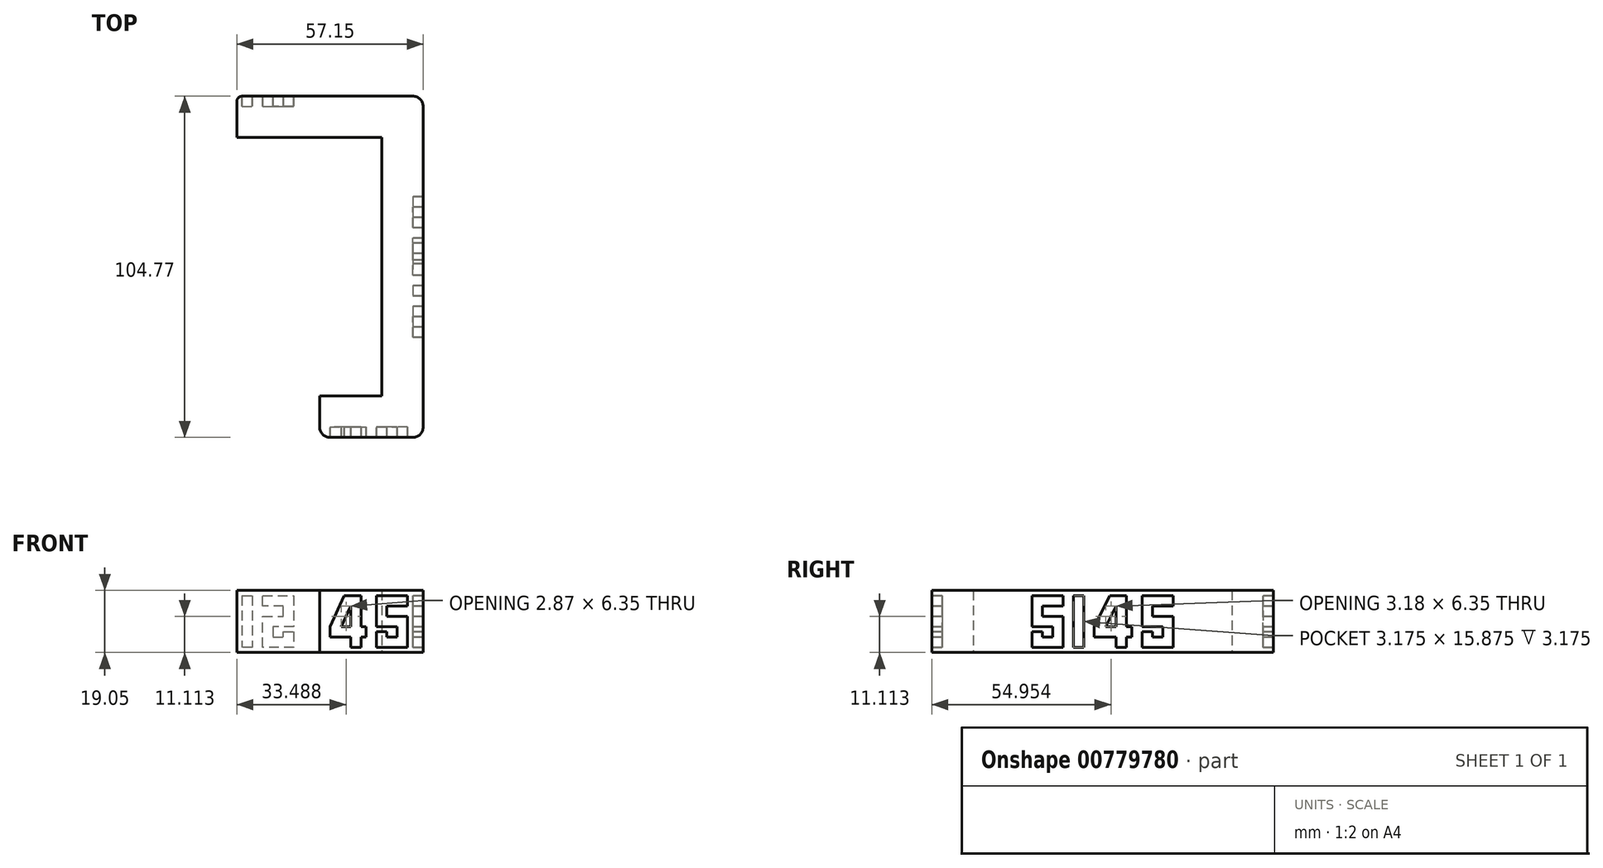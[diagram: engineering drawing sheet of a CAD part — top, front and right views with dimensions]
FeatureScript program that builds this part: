
annotation { "Feature Type Name" : "Feature", "Feature Type Description" : "" }
export const myFeature = defineFeature(function(context is Context, id is Id, definition is map)
    precondition{}
    {
        {
            var Q0;
            Q0=qCreatedBy(makeId("Top.planeOp"),FACE);
            var sketch = newSketch(context, id + "F0", { "sketchPlane" : qUnion([Q0])});
            skLineSegment(sketch, "E0", {"start": v(-261.38, 279.44) * mm, "end": v(-216.93, 279.44) * mm});
            skLineSegment(sketch, "E1", {"start": v(-216.93, 279.44) * mm, "end": v(-216.93, 200.07) * mm});
            skLineSegment(sketch, "E2", {"start": v(-216.93, 200.07) * mm, "end": v(-235.98, 200.07) * mm});
            skLineSegment(sketch, "E3", {"start": v(-235.98, 200.07) * mm, "end": v(-235.98, 187.37) * mm});
            skLineSegment(sketch, "E4", {"start": v(-235.98, 187.37) * mm, "end": v(-204.23, 187.37) * mm});
            skLineSegment(sketch, "E5", {"start": v(-204.23, 187.37) * mm, "end": v(-204.23, 292.14) * mm});
            skLineSegment(sketch, "E6", {"start": v(-204.23, 292.14) * mm, "end": v(-261.38, 292.14) * mm});
            skLineSegment(sketch, "E7", {"start": v(-261.38, 292.14) * mm, "end": v(-261.38, 279.44) * mm});
            skSolve(sketch);
        }
        {
            var Q0;
            Q0=makeQuery(id+"F0.imprint","IMPRINT",FACE,{"disambiguationData":[TD([[makeQuery(id+"F0.imprint","IMPRINT",EDGE,{"derivedFrom":sQuery(id+"F0.wireOp",EDGE,"E0")}),1.0]])]});
            extrude(context, id + "F1", {"entities" : qUnion([Q0]), "depth" : 19.05 * mm, "offsetDistance" : 25.4 * mm});
        }
        {
            var Q0;
            Q0=makeQuery(id+"F1.opExtrude","SWEPT_EDGE",EDGE,{"disambiguationData":[OSD([sQuery(id+"F0.wireOp",EDGE,"E4"),sQuery(id+"F0.wireOp",EDGE,"E5")])]});
            var Q1;
            Q1=makeQuery(id+"F1.opExtrude","SWEPT_EDGE",EDGE,{"disambiguationData":[OSD([sQuery(id+"F0.wireOp",EDGE,"E3"),sQuery(id+"F0.wireOp",EDGE,"E4")])]});
            var Q2;
            Q2=makeQuery(id+"F1.opExtrude","SWEPT_EDGE",EDGE,{"disambiguationData":[OSD([sQuery(id+"F0.wireOp",EDGE,"E5"),sQuery(id+"F0.wireOp",EDGE,"E6")])]});
            fillet(context, id + "F2", {"entities" : qUnion([Q0, Q1, Q2]), "radius" : 3.17 * mm, "tangentPropagation" : true, "allowEdgeOverflow" : false});
        }
        {
            var Q0;
            Q0=makeQuery(id+"F1.opExtrude","SWEPT_FACE",FACE,{"disambiguationData":[OSD([sQuery(id+"F0.wireOp",EDGE,"E4")])]});
            var sketch = newSketch(context, id + "F3", { "sketchPlane" : qUnion([Q0])});
            skLineSegment(sketch, "E8", {"start": v(-232.8, 7.94) * mm, "end": v(-232.8, 4.76) * mm});
            skLineSegment(sketch, "E9", {"start": v(-232.8, 4.76) * mm, "end": v(-226.46, 4.76) * mm});
            skLineSegment(sketch, "E10", {"start": v(-226.46, 4.76) * mm, "end": v(-226.46, 1.59) * mm});
            skLineSegment(sketch, "E11", {"start": v(-226.46, 1.59) * mm, "end": v(-223.28, 1.59) * mm});
            skLineSegment(sketch, "E12", {"start": v(-223.28, 1.59) * mm, "end": v(-223.28, 4.76) * mm});
            skLineSegment(sketch, "E13", {"start": v(-223.28, 4.76) * mm, "end": v(-221.7, 4.76) * mm});
            skLineSegment(sketch, "E14", {"start": v(-221.7, 4.76) * mm, "end": v(-221.7, 7.94) * mm});
            skLineSegment(sketch, "E15", {"start": v(-221.7, 7.94) * mm, "end": v(-223.28, 7.94) * mm});
            skLineSegment(sketch, "E16", {"start": v(-223.28, 7.94) * mm, "end": v(-223.28, 17.46) * mm});
            skLineSegment(sketch, "E17", {"start": v(-223.28, 17.46) * mm, "end": v(-228.5, 17.46) * mm});
            skLineSegment(sketch, "E18", {"start": v(-228.5, 17.46) * mm, "end": v(-232.8, 7.94) * mm});
            skLineSegment(sketch, "E19", {"start": v(-226.46, 7.94) * mm, "end": v(-229.33, 7.94) * mm});
            skLineSegment(sketch, "E20", {"start": v(-229.33, 7.94) * mm, "end": v(-226.46, 14.29) * mm});
            skLineSegment(sketch, "E21", {"start": v(-226.46, 14.29) * mm, "end": v(-226.46, 7.94) * mm});
            skLineSegment(sketch, "E22", {"start": v(-209, 17.46) * mm, "end": v(-218.52, 17.46) * mm});
            skLineSegment(sketch, "E23", {"start": v(-218.52, 17.46) * mm, "end": v(-218.52, 7.94) * mm});
            skLineSegment(sketch, "E24", {"start": v(-218.52, 7.94) * mm, "end": v(-212.17, 7.94) * mm});
            skLineSegment(sketch, "E25", {"start": v(-212.17, 7.94) * mm, "end": v(-212.17, 4.76) * mm});
            skLineSegment(sketch, "E26", {"start": v(-212.17, 4.76) * mm, "end": v(-215.35, 4.76) * mm});
            skPoint(sketch, "E26.endSnap0", {"position": v(-215.35, 7.94) * mm});
            skLineSegment(sketch, "E27", {"start": v(-215.35, 4.76) * mm, "end": v(-215.35, 6.35) * mm});
            skPoint(sketch, "E27.endSnap0", {"position": v(-212.17, 6.35) * mm});
            skLineSegment(sketch, "E28", {"start": v(-215.35, 6.35) * mm, "end": v(-218.52, 6.35) * mm});
            skLineSegment(sketch, "E29", {"start": v(-218.52, 6.35) * mm, "end": v(-218.52, 1.59) * mm});
            skLineSegment(sketch, "E30", {"start": v(-218.52, 1.59) * mm, "end": v(-209, 1.59) * mm});
            skLineSegment(sketch, "E31", {"start": v(-209, 1.59) * mm, "end": v(-209, 11.11) * mm});
            skLineSegment(sketch, "E32", {"start": v(-209, 11.11) * mm, "end": v(-215.35, 11.11) * mm});
            skLineSegment(sketch, "E33", {"start": v(-215.35, 11.11) * mm, "end": v(-215.35, 14.29) * mm});
            skLineSegment(sketch, "E34", {"start": v(-215.35, 14.29) * mm, "end": v(-209, 14.29) * mm});
            skLineSegment(sketch, "E35", {"start": v(-209, 14.29) * mm, "end": v(-209, 17.46) * mm});
            skSolve(sketch);
        }
        {
            var Q0;
            Q0=makeQuery(id+"F3.imprint","IMPRINT",FACE,{"disambiguationData":[TD([[makeQuery(id+"F3.imprint","IMPRINT",EDGE,{"derivedFrom":sQuery(id+"F3.wireOp",EDGE,"E8")}),1.0]])]});
            var Q1;
            Q1=makeQuery(id+"F3.imprint","IMPRINT",FACE,{"disambiguationData":[TD([[makeQuery(id+"F3.imprint","IMPRINT",EDGE,{"derivedFrom":sQuery(id+"F3.wireOp",EDGE,"E22")}),1.0]])]});
            extrude(context, id + "F4", {"entities" : qUnion([Q0, Q1]), "operationType" : NewBodyOperationType.REMOVE, "oppositeDirection" : true, "depth" : 3.17 * mm, "offsetDistance" : 25.4 * mm});
        }
        {
            var Q0;
            Q0=makeQuery(id+"F1.opExtrude","SWEPT_FACE",FACE,{"disambiguationData":[OSD([sQuery(id+"F0.wireOp",EDGE,"E5")])]});
            var sketch = newSketch(context, id + "F5", { "sketchPlane" : qUnion([Q0])});
            skLineSegment(sketch, "E36", {"start": v(227.66, 17.46) * mm, "end": v(218.14, 17.46) * mm});
            skLineSegment(sketch, "E37", {"start": v(218.14, 17.46) * mm, "end": v(218.14, 7.94) * mm});
            skLineSegment(sketch, "E38", {"start": v(218.14, 7.94) * mm, "end": v(224.49, 7.94) * mm});
            skLineSegment(sketch, "E39", {"start": v(224.49, 7.94) * mm, "end": v(224.49, 4.76) * mm});
            skLineSegment(sketch, "E40", {"start": v(224.49, 4.76) * mm, "end": v(221.31, 4.76) * mm});
            skLineSegment(sketch, "E41", {"start": v(221.31, 4.76) * mm, "end": v(221.31, 6.35) * mm});
            skLineSegment(sketch, "E42", {"start": v(221.31, 6.35) * mm, "end": v(218.14, 6.35) * mm});
            skLineSegment(sketch, "E43", {"start": v(218.14, 6.35) * mm, "end": v(218.14, 1.59) * mm});
            skLineSegment(sketch, "E44", {"start": v(218.14, 1.59) * mm, "end": v(227.66, 1.59) * mm});
            skLineSegment(sketch, "E45", {"start": v(227.66, 1.59) * mm, "end": v(227.66, 11.11) * mm});
            skLineSegment(sketch, "E46", {"start": v(227.66, 11.11) * mm, "end": v(221.31, 11.11) * mm});
            skLineSegment(sketch, "E47", {"start": v(221.31, 11.11) * mm, "end": v(221.31, 14.29) * mm});
            skLineSegment(sketch, "E48", {"start": v(221.31, 14.29) * mm, "end": v(227.66, 14.29) * mm});
            skLineSegment(sketch, "E49", {"start": v(227.66, 14.29) * mm, "end": v(227.66, 17.46) * mm});
            skLineSegment(sketch, "E50", {"start": v(230.84, 17.46) * mm, "end": v(230.84, 1.59) * mm});
            skLineSegment(sketch, "E51", {"start": v(230.84, 1.59) * mm, "end": v(234.01, 1.59) * mm});
            skLineSegment(sketch, "E52", {"start": v(234.01, 1.59) * mm, "end": v(234.01, 17.46) * mm});
            skLineSegment(sketch, "E53", {"start": v(234.01, 17.46) * mm, "end": v(230.84, 17.46) * mm});
            skLineSegment(sketch, "E54", {"start": v(247.09, 17.46) * mm, "end": v(241.95, 17.46) * mm});
            skLineSegment(sketch, "E55", {"start": v(241.95, 17.46) * mm, "end": v(237.19, 7.94) * mm});
            skLineSegment(sketch, "E56", {"start": v(237.19, 7.94) * mm, "end": v(237.19, 4.76) * mm});
            skLineSegment(sketch, "E57", {"start": v(237.19, 4.76) * mm, "end": v(243.91, 4.76) * mm});
            skLineSegment(sketch, "E58", {"start": v(243.91, 4.76) * mm, "end": v(243.91, 1.59) * mm});
            skLineSegment(sketch, "E59", {"start": v(243.91, 1.59) * mm, "end": v(247.09, 1.59) * mm});
            skLineSegment(sketch, "E60", {"start": v(247.09, 1.59) * mm, "end": v(247.09, 4.76) * mm});
            skLineSegment(sketch, "E61", {"start": v(247.09, 4.76) * mm, "end": v(248.67, 4.76) * mm});
            skLineSegment(sketch, "E62", {"start": v(248.67, 4.76) * mm, "end": v(248.67, 7.94) * mm});
            skLineSegment(sketch, "E63", {"start": v(248.67, 7.94) * mm, "end": v(247.09, 7.94) * mm});
            skLineSegment(sketch, "E64", {"start": v(247.09, 7.94) * mm, "end": v(247.09, 17.46) * mm});
            skLineSegment(sketch, "E65", {"start": v(261.37, 17.46) * mm, "end": v(251.85, 17.46) * mm});
            skLineSegment(sketch, "E66", {"start": v(251.85, 17.46) * mm, "end": v(251.85, 7.94) * mm});
            skLineSegment(sketch, "E67", {"start": v(251.85, 7.94) * mm, "end": v(258.2, 7.94) * mm});
            skLineSegment(sketch, "E68", {"start": v(258.2, 7.94) * mm, "end": v(258.2, 4.76) * mm});
            skLineSegment(sketch, "E69", {"start": v(258.2, 4.76) * mm, "end": v(255.02, 4.76) * mm});
            skLineSegment(sketch, "E70", {"start": v(255.02, 4.76) * mm, "end": v(255.02, 6.35) * mm});
            skLineSegment(sketch, "E71", {"start": v(255.02, 6.35) * mm, "end": v(251.85, 6.35) * mm});
            skLineSegment(sketch, "E72", {"start": v(251.85, 6.35) * mm, "end": v(251.85, 1.59) * mm});
            skLineSegment(sketch, "E73", {"start": v(251.85, 1.59) * mm, "end": v(261.37, 1.59) * mm});
            skLineSegment(sketch, "E74", {"start": v(261.37, 1.59) * mm, "end": v(261.37, 11.11) * mm});
            skLineSegment(sketch, "E75", {"start": v(261.37, 11.11) * mm, "end": v(255.02, 11.11) * mm});
            skLineSegment(sketch, "E76", {"start": v(255.02, 11.11) * mm, "end": v(255.02, 14.29) * mm});
            skLineSegment(sketch, "E77", {"start": v(255.02, 14.29) * mm, "end": v(261.37, 14.29) * mm});
            skLineSegment(sketch, "E78", {"start": v(261.37, 14.29) * mm, "end": v(261.37, 17.46) * mm});
            skLineSegment(sketch, "E79", {"start": v(243.91, 7.94) * mm, "end": v(240.74, 7.94) * mm});
            skLineSegment(sketch, "E80", {"start": v(240.74, 7.94) * mm, "end": v(243.91, 14.29) * mm});
            skLineSegment(sketch, "E81", {"start": v(243.91, 14.29) * mm, "end": v(243.91, 7.94) * mm});
            skLineSegment(sketch, "E82", {"start": v(261.37, 17.46) * mm, "end": v(288.97, 17.46) * mm});
            skLineSegment(sketch, "E83", {"start": v(218.14, 17.46) * mm, "end": v(190.54, 17.46) * mm});
            skSolve(sketch);
        }
        {
            var Q0;
            Q0=makeQuery(id+"F5.imprint","IMPRINT",FACE,{"disambiguationData":[TD([[makeQuery(id+"F5.imprint","IMPRINT",EDGE,{"derivedFrom":sQuery(id+"F5.wireOp",EDGE,"E36")}),1.0]])]});
            var Q1;
            Q1=makeQuery(id+"F5.imprint","IMPRINT",FACE,{"disambiguationData":[TD([[makeQuery(id+"F5.imprint","IMPRINT",EDGE,{"derivedFrom":sQuery(id+"F5.wireOp",EDGE,"E50")}),1.0]])]});
            var Q2;
            Q2=makeQuery(id+"F5.imprint","IMPRINT",FACE,{"disambiguationData":[TD([[makeQuery(id+"F5.imprint","IMPRINT",EDGE,{"derivedFrom":sQuery(id+"F5.wireOp",EDGE,"E54")}),1.0]])]});
            var Q3;
            Q3=makeQuery(id+"F5.imprint","IMPRINT",FACE,{"disambiguationData":[TD([[makeQuery(id+"F5.imprint","IMPRINT",EDGE,{"derivedFrom":sQuery(id+"F5.wireOp",EDGE,"E65")}),1.0]])]});
            extrude(context, id + "F6", {"entities" : qUnion([Q0, Q1, Q2, Q3]), "operationType" : NewBodyOperationType.REMOVE, "oppositeDirection" : true, "depth" : 3.17 * mm, "offsetDistance" : 25.4 * mm});
        }
        {
            var Q0;
            Q0=makeQuery(id+"F4.boolean.opBoolean","COPY",FACE,{"derivedFrom":makeQuery(id+"F4.opExtrude","CAP_FACE",FACE,{"disambiguationData":[OSD([sQuery(id+"F3.wireOp",EDGE,"E8"),sQuery(id+"F3.wireOp",EDGE,"E9"),sQuery(id+"F3.wireOp",EDGE,"E10"),sQuery(id+"F3.wireOp",EDGE,"E11"),sQuery(id+"F3.wireOp",EDGE,"E12"),sQuery(id+"F3.wireOp",EDGE,"E13"),sQuery(id+"F3.wireOp",EDGE,"E14"),sQuery(id+"F3.wireOp",EDGE,"E15"),sQuery(id+"F3.wireOp",EDGE,"E16"),sQuery(id+"F3.wireOp",EDGE,"E17"),sQuery(id+"F3.wireOp",EDGE,"E18"),sQuery(id+"F3.wireOp",EDGE,"E19"),sQuery(id+"F3.wireOp",EDGE,"E20"),sQuery(id+"F3.wireOp",EDGE,"E21")])],"isStart":false})});
            var Q1;
            Q1=makeQuery(id+"F4.boolean.opBoolean","COPY",FACE,{"derivedFrom":makeQuery(id+"F4.opExtrude","CAP_FACE",FACE,{"disambiguationData":[OSD([sQuery(id+"F3.wireOp",EDGE,"E22"),sQuery(id+"F3.wireOp",EDGE,"E23"),sQuery(id+"F3.wireOp",EDGE,"E24"),sQuery(id+"F3.wireOp",EDGE,"E25"),sQuery(id+"F3.wireOp",EDGE,"E26"),sQuery(id+"F3.wireOp",EDGE,"E27"),sQuery(id+"F3.wireOp",EDGE,"E28"),sQuery(id+"F3.wireOp",EDGE,"E29"),sQuery(id+"F3.wireOp",EDGE,"E30"),sQuery(id+"F3.wireOp",EDGE,"E31"),sQuery(id+"F3.wireOp",EDGE,"E32"),sQuery(id+"F3.wireOp",EDGE,"E33"),sQuery(id+"F3.wireOp",EDGE,"E34"),sQuery(id+"F3.wireOp",EDGE,"E35")])],"isStart":false})});
            extrude(context, id + "F7", {"entities" : qUnion([Q0, Q1]), "depth" : 3.15 * mm, "offsetDistance" : 25.4 * mm});
        }
        {
            var Q0;
            Q0=makeQuery(id+"F6.boolean.opBoolean","COPY",FACE,{"derivedFrom":makeQuery(id+"F6.opExtrude","CAP_FACE",FACE,{"disambiguationData":[OSD([sQuery(id+"F5.wireOp",EDGE,"E36"),sQuery(id+"F5.wireOp",EDGE,"E37"),sQuery(id+"F5.wireOp",EDGE,"E38"),sQuery(id+"F5.wireOp",EDGE,"E39"),sQuery(id+"F5.wireOp",EDGE,"E40"),sQuery(id+"F5.wireOp",EDGE,"E41"),sQuery(id+"F5.wireOp",EDGE,"E42"),sQuery(id+"F5.wireOp",EDGE,"E43"),sQuery(id+"F5.wireOp",EDGE,"E44"),sQuery(id+"F5.wireOp",EDGE,"E45"),sQuery(id+"F5.wireOp",EDGE,"E46"),sQuery(id+"F5.wireOp",EDGE,"E47"),sQuery(id+"F5.wireOp",EDGE,"E48"),sQuery(id+"F5.wireOp",EDGE,"E49")])],"isStart":false})});
            var Q1;
            Q1=makeQuery(id+"F6.boolean.opBoolean","COPY",FACE,{"derivedFrom":makeQuery(id+"F6.opExtrude","CAP_FACE",FACE,{"disambiguationData":[OSD([sQuery(id+"F5.wireOp",EDGE,"E50"),sQuery(id+"F5.wireOp",EDGE,"E51"),sQuery(id+"F5.wireOp",EDGE,"E52"),sQuery(id+"F5.wireOp",EDGE,"E53")])],"isStart":false})});
            var Q2;
            Q2=makeQuery(id+"F6.boolean.opBoolean","COPY",FACE,{"derivedFrom":makeQuery(id+"F6.opExtrude","CAP_FACE",FACE,{"disambiguationData":[OSD([sQuery(id+"F5.wireOp",EDGE,"E54"),sQuery(id+"F5.wireOp",EDGE,"E55"),sQuery(id+"F5.wireOp",EDGE,"E56"),sQuery(id+"F5.wireOp",EDGE,"E57"),sQuery(id+"F5.wireOp",EDGE,"E58"),sQuery(id+"F5.wireOp",EDGE,"E59"),sQuery(id+"F5.wireOp",EDGE,"E60"),sQuery(id+"F5.wireOp",EDGE,"E61"),sQuery(id+"F5.wireOp",EDGE,"E62"),sQuery(id+"F5.wireOp",EDGE,"E63"),sQuery(id+"F5.wireOp",EDGE,"E64"),sQuery(id+"F5.wireOp",EDGE,"E79"),sQuery(id+"F5.wireOp",EDGE,"E80"),sQuery(id+"F5.wireOp",EDGE,"E81")])],"isStart":false})});
            var Q3;
            Q3=makeQuery(id+"F6.boolean.opBoolean","COPY",FACE,{"derivedFrom":makeQuery(id+"F6.opExtrude","CAP_FACE",FACE,{"disambiguationData":[OSD([sQuery(id+"F5.wireOp",EDGE,"E65"),sQuery(id+"F5.wireOp",EDGE,"E66"),sQuery(id+"F5.wireOp",EDGE,"E67"),sQuery(id+"F5.wireOp",EDGE,"E68"),sQuery(id+"F5.wireOp",EDGE,"E69"),sQuery(id+"F5.wireOp",EDGE,"E70"),sQuery(id+"F5.wireOp",EDGE,"E71"),sQuery(id+"F5.wireOp",EDGE,"E72"),sQuery(id+"F5.wireOp",EDGE,"E73"),sQuery(id+"F5.wireOp",EDGE,"E74"),sQuery(id+"F5.wireOp",EDGE,"E75"),sQuery(id+"F5.wireOp",EDGE,"E76"),sQuery(id+"F5.wireOp",EDGE,"E77"),sQuery(id+"F5.wireOp",EDGE,"E78")])],"isStart":false})});
            extrude(context, id + "F8", {"entities" : qUnion([Q0, Q1, Q2, Q3]), "depth" : 3.15 * mm, "offsetDistance" : 25.4 * mm});
        }
        {
            var Q0;
            Q0=makeQuery(id+"F1.opExtrude","SWEPT_EDGE",EDGE,{"disambiguationData":[OSD([sQuery(id+"F0.wireOp",EDGE,"E6"),sQuery(id+"F0.wireOp",EDGE,"E7")])]});
            fillet(context, id + "F9", {"entities" : qUnion([Q0]), "radius" : 1.59 * mm, "tangentPropagation" : true, "allowEdgeOverflow" : false});
        }
        {
            var Q0;
            Q0=makeQuery(id+"F1.opExtrude","SWEPT_FACE",FACE,{"disambiguationData":[OSD([sQuery(id+"F0.wireOp",EDGE,"E6")])]});
            var sketch = newSketch(context, id + "F10", { "sketchPlane" : qUnion([Q0])});
            skLineSegment(sketch, "E84", {"start": v(259.8, 17.46) * mm, "end": v(256.62, 17.46) * mm});
            skLineSegment(sketch, "E85", {"start": v(256.62, 17.46) * mm, "end": v(256.62, 1.59) * mm});
            skLineSegment(sketch, "E86", {"start": v(256.62, 1.59) * mm, "end": v(259.8, 1.59) * mm});
            skLineSegment(sketch, "E87", {"start": v(259.8, 1.59) * mm, "end": v(259.8, 17.46) * mm});
            skLineSegment(sketch, "E88", {"start": v(253.45, 17.46) * mm, "end": v(243.92, 17.46) * mm});
            skLineSegment(sketch, "E89", {"start": v(243.92, 17.46) * mm, "end": v(243.92, 7.94) * mm});
            skLineSegment(sketch, "E90", {"start": v(243.92, 7.94) * mm, "end": v(250.27, 7.94) * mm});
            skLineSegment(sketch, "E91", {"start": v(250.27, 7.94) * mm, "end": v(250.27, 4.76) * mm});
            skLineSegment(sketch, "E92", {"start": v(250.27, 4.76) * mm, "end": v(247.1, 4.76) * mm});
            skLineSegment(sketch, "E93", {"start": v(247.1, 4.76) * mm, "end": v(247.1, 6.35) * mm});
            skLineSegment(sketch, "E94", {"start": v(247.1, 6.35) * mm, "end": v(243.92, 6.35) * mm});
            skLineSegment(sketch, "E95", {"start": v(243.92, 6.35) * mm, "end": v(243.92, 1.59) * mm});
            skLineSegment(sketch, "E96", {"start": v(243.92, 1.59) * mm, "end": v(253.45, 1.59) * mm});
            skLineSegment(sketch, "E97", {"start": v(253.45, 1.59) * mm, "end": v(253.45, 11.11) * mm});
            skLineSegment(sketch, "E98", {"start": v(253.45, 11.11) * mm, "end": v(247.1, 11.11) * mm});
            skLineSegment(sketch, "E99", {"start": v(247.1, 11.11) * mm, "end": v(247.1, 14.29) * mm});
            skLineSegment(sketch, "E100", {"start": v(247.1, 14.29) * mm, "end": v(253.45, 14.29) * mm});
            skLineSegment(sketch, "E101", {"start": v(253.45, 14.29) * mm, "end": v(253.45, 17.46) * mm});
            skSolve(sketch);
        }
        {
            var Q0;
            Q0=makeQuery(id+"F10.imprint","IMPRINT",FACE,{"disambiguationData":[TD([[makeQuery(id+"F10.imprint","IMPRINT",EDGE,{"derivedFrom":sQuery(id+"F10.wireOp",EDGE,"E88")}),1.0]])]});
            var Q1;
            Q1=makeQuery(id+"F10.imprint","IMPRINT",FACE,{"disambiguationData":[TD([[makeQuery(id+"F10.imprint","IMPRINT",EDGE,{"derivedFrom":sQuery(id+"F10.wireOp",EDGE,"E84")}),1.0]])]});
            extrude(context, id + "F11", {"entities" : qUnion([Q0, Q1]), "operationType" : NewBodyOperationType.REMOVE, "oppositeDirection" : true, "depth" : 3.17 * mm, "offsetDistance" : 25.4 * mm});
        }
        {
            var Q0;
            Q0=makeQuery(id+"F11.boolean.opBoolean","COPY",FACE,{"derivedFrom":makeQuery(id+"F11.opExtrude","CAP_FACE",FACE,{"disambiguationData":[OSD([sQuery(id+"F10.wireOp",EDGE,"E88"),sQuery(id+"F10.wireOp",EDGE,"E89"),sQuery(id+"F10.wireOp",EDGE,"E90"),sQuery(id+"F10.wireOp",EDGE,"E91"),sQuery(id+"F10.wireOp",EDGE,"E92"),sQuery(id+"F10.wireOp",EDGE,"E93"),sQuery(id+"F10.wireOp",EDGE,"E94"),sQuery(id+"F10.wireOp",EDGE,"E95"),sQuery(id+"F10.wireOp",EDGE,"E96"),sQuery(id+"F10.wireOp",EDGE,"E97"),sQuery(id+"F10.wireOp",EDGE,"E98"),sQuery(id+"F10.wireOp",EDGE,"E99"),sQuery(id+"F10.wireOp",EDGE,"E100"),sQuery(id+"F10.wireOp",EDGE,"E101")])],"isStart":false})});
            var Q1;
            Q1=makeQuery(id+"F11.boolean.opBoolean","COPY",FACE,{"derivedFrom":makeQuery(id+"F11.opExtrude","CAP_FACE",FACE,{"disambiguationData":[OSD([sQuery(id+"F10.wireOp",EDGE,"E84"),sQuery(id+"F10.wireOp",EDGE,"E85"),sQuery(id+"F10.wireOp",EDGE,"E86"),sQuery(id+"F10.wireOp",EDGE,"E87")])],"isStart":false})});
            extrude(context, id + "F12", {"entities" : qUnion([Q0, Q1]), "depth" : 3.15 * mm, "offsetDistance" : 25.4 * mm});
        }
    });
